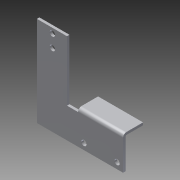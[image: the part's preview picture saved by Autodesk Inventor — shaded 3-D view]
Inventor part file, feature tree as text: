
AUTODESK INVENTOR PART (.ipt)
format: ipt  version: 2013 (Build 170138000, 138)  size: 173,568 bytes
history: native  units: in
note: dims shown in document units (in); Inventor stores cm internally (conversion verified against a paired STEP export)
features: sketch x7, other x6, sheet_metal_op x4, reference x4, extrude x2
ambient origin geometry x8: Origin, YZ Plane, XZ Plane, XY Plane, X Axis, Y Axis, Z Axis, Center Point
bodies: Solid1 (feature_tree)
feature tree (23):
  sheet_metal_op  "Face1"
  sheet_metal_op  "Flange1"
  extrude  "Extrusion1"  Depth=1.5in
  extrude  "Extrusion3"  Depth=1.181in
  sketch  "Sketch1"  dims[d1=4.297in d2=1.5in]
  other  "Plate1"
  sketch  "Sketch2"  dims[d3=0.295in d4=1.181in]
  other  "Plate2"
  sheet_metal_op  "Bend1"
  sheet_metal_op  "Corner1"
  sketch  "Sketch8"  dims[d5=0.295in]
  reference  "Reference1"
  reference  "Reference2"
  sketch  "Sketch10"  dims[d8=0.125in]
  sketch  "Sketch15"  dims[d9=0.125in]
  sketch  "Sketch16"  dims[d10=0.0625in]
  reference  "Reference7"
  reference  "Reference8"
  sketch  "Sketch17"  dims[d11=0.25in d12=0.125in d13=1.0in d14=90.0deg d15=0.05in d16=0.5in d17=0.125in d18=0.125in d19=0.125in d20=0.0in d21=2.0in d22=2.053in d23=1.0in d24=0.0in d31=3.0in d32=0.0in d33=0.125in d34=0.0in d35=1.5in d36=0.125in d37=0.0in]
  other  "Cut1"
  other  "Cut4"
  other  "Cut5"
  other  "Definition1"
